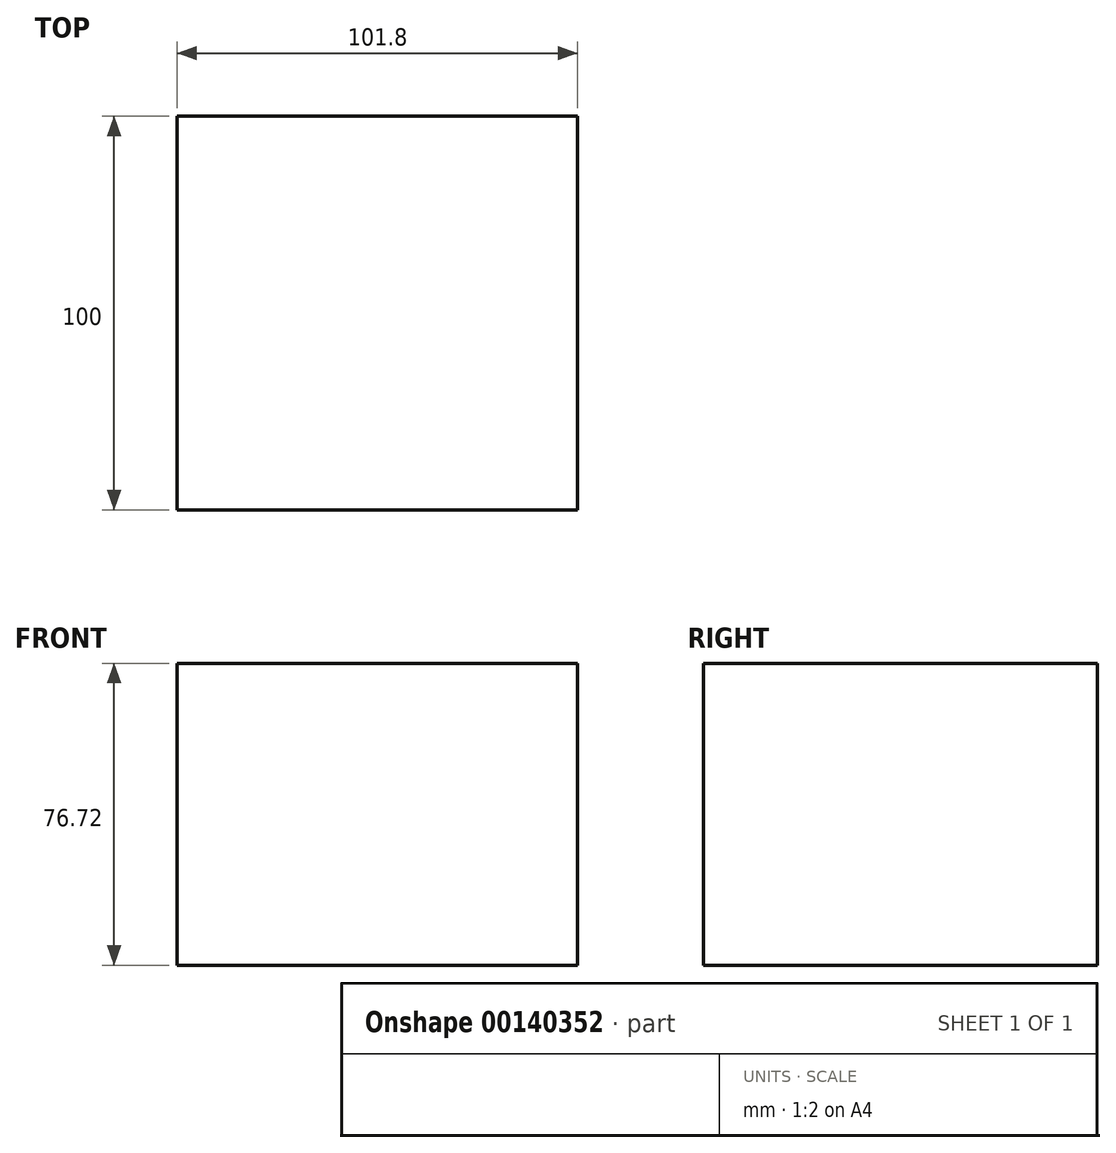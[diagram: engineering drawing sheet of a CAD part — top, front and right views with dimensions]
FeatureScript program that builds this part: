
annotation { "Feature Type Name" : "Feature", "Feature Type Description" : "" }
export const myFeature = defineFeature(function(context is Context, id is Id, definition is map)
    precondition{}
    {
        {
            var Q0;
            Q0=qCreatedBy(makeId("Front.planeOp"),FACE);
            var sketch = newSketch(context, id + "F0", { "sketchPlane" : qUnion([Q0])});
            skLineSegment(sketch, "E0.bottom", {"start": v(-50.9, 38.36) * mm, "end": v(50.9, 38.36) * mm});
            skLineSegment(sketch, "E0.top", {"start": v(-50.9, -38.36) * mm, "end": v(50.9, -38.36) * mm});
            skLineSegment(sketch, "E0.left", {"start": v(-50.9, 38.36) * mm, "end": v(-50.9, -38.36) * mm});
            skLineSegment(sketch, "E0.right", {"start": v(50.9, 38.36) * mm, "end": v(50.9, -38.36) * mm});
            skPoint(sketch, "E0.middle", {"position": v(0, 0) * mm});
            skSolve(sketch);
        }
        {
            var Q0;
            Q0 = qSketchRegion(id + "F0", true);
            extrude(context, id + "F1", {"entities" : qUnion([Q0]), "depth" : 100 * mm});
        }
    });
